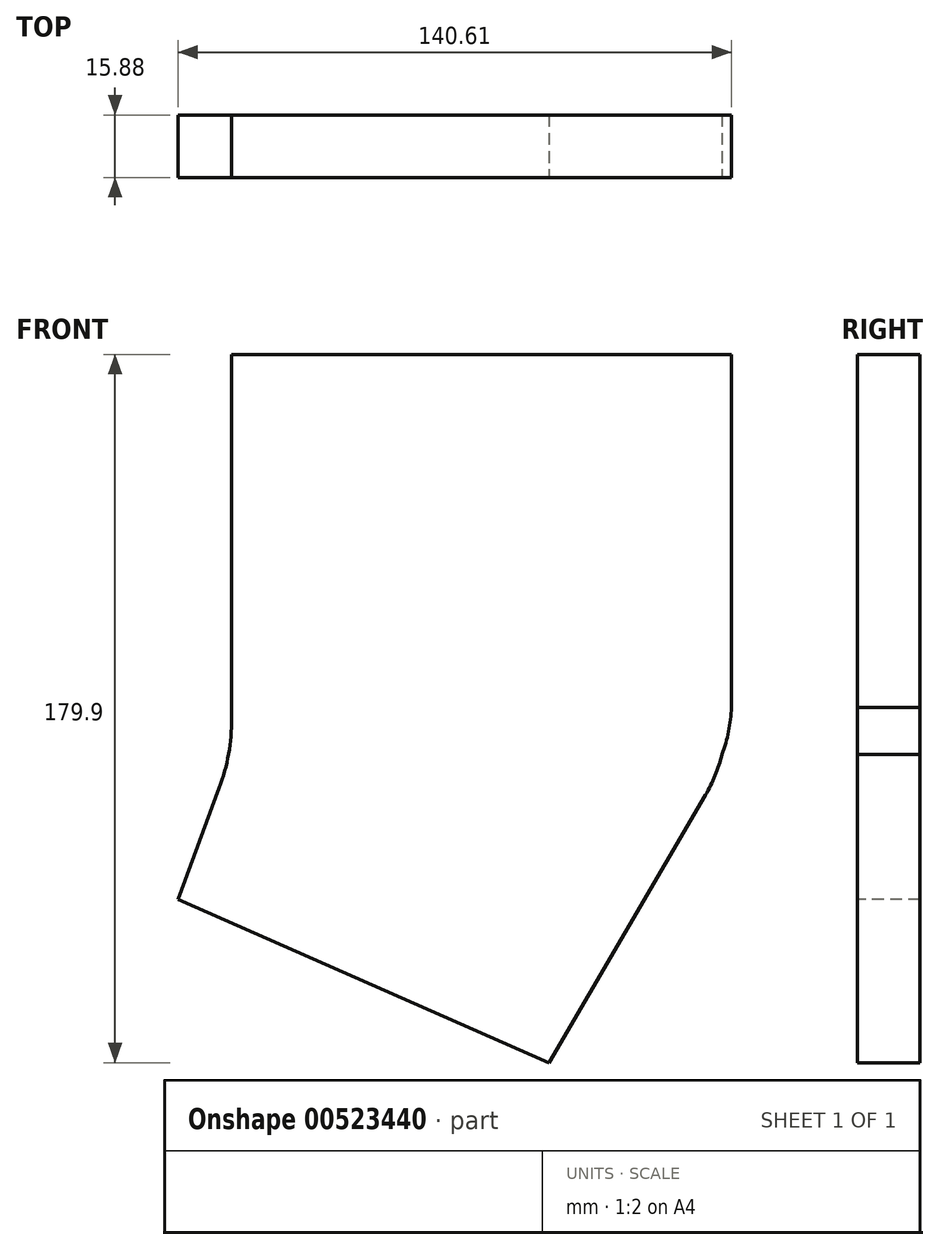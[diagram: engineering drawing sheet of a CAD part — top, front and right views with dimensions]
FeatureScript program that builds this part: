
annotation { "Feature Type Name" : "Feature", "Feature Type Description" : "" }
export const myFeature = defineFeature(function(context is Context, id is Id, definition is map)
    precondition{}
    {
        {
            var Q0;
            Q0=qCreatedBy(makeId("Front.planeOp"),FACE);
            var sketch = newSketch(context, id + "F0", { "sketchPlane" : qUnion([Q0])});
            skLineSegment(sketch, "E0.bottom", {"start": v(-125.6, 9.55) * mm, "end": v(1.4, 9.55) * mm});
            skLineSegment(sketch, "E0.top", {"start": v(-125.6, -92.05) * mm, "end": v(1.4, -92.05) * mm});
            skLineSegment(sketch, "E0.left", {"start": v(-125.6, 9.55) * mm, "end": v(-125.6, -92.05) * mm});
            skLineSegment(sketch, "E0.right", {"start": v(1.4, 9.55) * mm, "end": v(1.4, -92.05) * mm});
            skSolve(sketch);
        }
        {
            var Q0;
            Q0 = qSketchRegion(id + "F0", true);
            extrude(context, id + "F1", {"entities" : qUnion([Q0]), "depth" : 15.88 * mm, "offsetDistance" : 25.4 * mm});
        }
        {
            var Q0;
            Q0=makeQuery(id+"F1.opExtrude","CAP_FACE",FACE,{"disambiguationData":[OSD([sQuery(id+"F0.wireOp",EDGE,"E0.bottom"),sQuery(id+"F0.wireOp",EDGE,"E0.top"),sQuery(id+"F0.wireOp",EDGE,"E0.left"),sQuery(id+"F0.wireOp",EDGE,"E0.right")])],"isStart":false});
            var sketch = newSketch(context, id + "F2", { "sketchPlane" : qUnion([Q0])});
            skLineSegment(sketch, "E1", {"start": v(1.4, -92.05) * mm, "end": v(1.4, -75.45) * mm});
            skLineSegment(sketch, "E2", {"start": v(-1.03, -92.05) * mm, "end": v(1.4, -92.05) * mm});
            skArc(sketch, "E3", {"start": v(-1.03, -92.05) * mm, "mid": v(1.03, -83.87) * mm, "end": v(1.4, -75.45) * mm});
            skSolve(sketch);
        }
        {
            var Q0;
            Q0 = qSketchRegion(id + "F2", true);
            extrude(context, id + "F3", {"entities" : qUnion([Q0]), "operationType" : NewBodyOperationType.REMOVE, "oppositeDirection" : true, "depth" : 19.05 * mm, "offsetDistance" : 25.4 * mm});
        }
        {
            var Q0;
            Q0=makeQuery(id+"F1.opExtrude","CAP_FACE",FACE,{"disambiguationData":[OSD([sQuery(id+"F0.wireOp",EDGE,"E0.bottom"),sQuery(id+"F0.wireOp",EDGE,"E0.top"),sQuery(id+"F0.wireOp",EDGE,"E0.left"),sQuery(id+"F0.wireOp",EDGE,"E0.right")])],"isStart":false});
            var sketch = newSketch(context, id + "F4", { "sketchPlane" : qUnion([Q0])});
            skLineSegment(sketch, "E4", {"start": v(-125.6, -92.05) * mm, "end": v(-139.21, -128.83) * mm});
            skLineSegment(sketch, "E5", {"start": v(-5.27, -102.37) * mm, "end": v(-44.97, -170.35) * mm});
            skLineSegment(sketch, "E6", {"start": v(-44.97, -170.35) * mm, "end": v(-139.21, -128.83) * mm});
            skLineSegment(sketch, "E7", {"start": v(-125.6, -92.05) * mm, "end": v(-1.03, -92.05) * mm});
            skArc(sketch, "E8", {"start": v(-5.27, -102.37) * mm, "mid": v(-2.79, -97.36) * mm, "end": v(-1.03, -92.05) * mm});
            skSolve(sketch);
        }
        {
            var Q0;
            Q0 = qSketchRegion(id + "F4", true);
            extrude(context, id + "F5", {"entities" : qUnion([Q0]), "operationType" : NewBodyOperationType.ADD, "oppositeDirection" : true, "depth" : 15.88 * mm, "offsetDistance" : 25.4 * mm});
        }
        {
            var Q0;
            {var subQ0=sQuery(id+"F0.wireOp",EDGE,"E0.left");Q0=makeQuery(id+"F5.boolean.opBoolean","MERGE",EDGE,{"derivedFrom":[makeQuery(id+"F1.opExtrude","SWEPT_EDGE",EDGE,{"disambiguationData":[OSD([sQuery(id+"F0.wireOp",EDGE,"E0.top"),subQ0])]}),makeQuery(id+"F5.opExtrude","SWEPT_EDGE",EDGE,{"disambiguationData":[OSD([subQ0,sQuery(id+"F4.wireOp",EDGE,"E4"),sQuery(id+"F4.wireOp",EDGE,"E7")])]})]});}
            fillet(context, id + "F6", {"entities" : qUnion([Q0]), "radius" : 50.8 * mm, "tangentPropagation" : true, "allowEdgeOverflow" : false});
        }
    });
